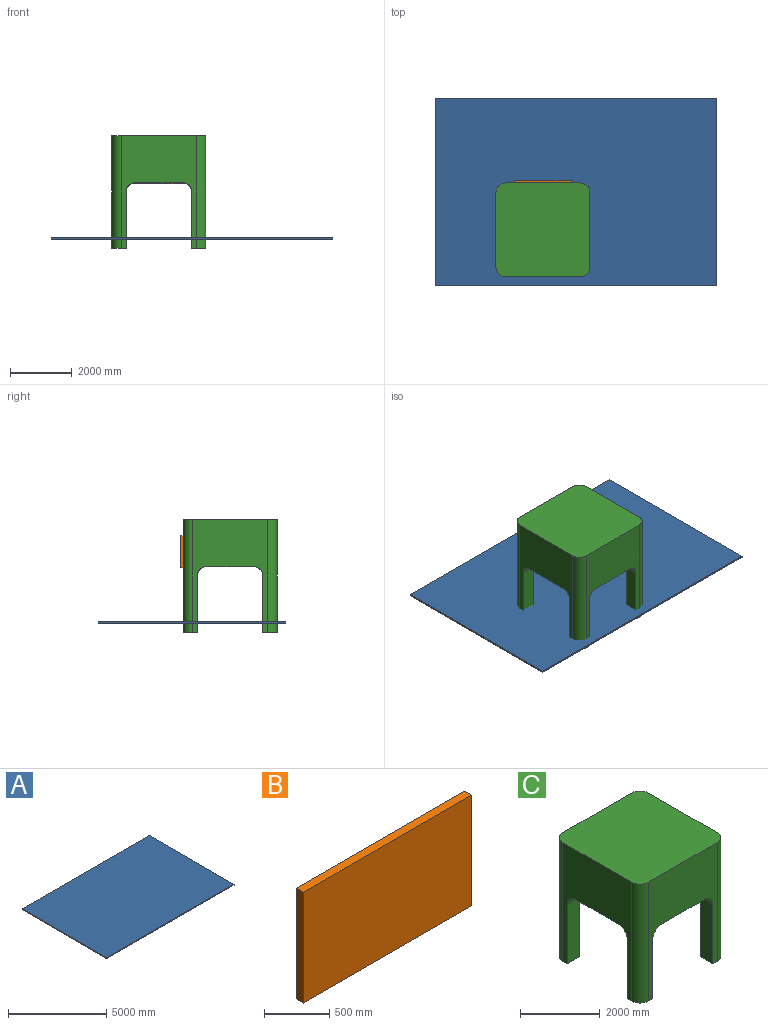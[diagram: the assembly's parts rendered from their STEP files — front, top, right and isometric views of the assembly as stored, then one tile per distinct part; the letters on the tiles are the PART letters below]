
ASSEMBLY  parts=3 mates=3
PART A: 6 faces, bbox 9144x6096x50.8 mm
  f0: plane 9144x50.8mm, normal (0,1,0), area 464515.2mm2, adj f1,f3,f4,f5
  f1: plane 6096x50.8mm, normal (-1,0,0), area 309676.8mm2, adj f0,f2,f4,f5
  f2: plane 9144x50.8mm, normal (0,-1,0), area 464515.2mm2, adj f1,f3,f4,f5
  f3: plane 6096x50.8mm, normal (1,0,0), area 309676.8mm2, adj f0,f2,f4,f5
  f4: plane 9144x6096mm, normal (0,0,1), area 55741824mm2, adj f0,f1,f2,f3
  f5: plane 9144x6096mm, normal (0,0,-1), area 55741824mm2, adj f0,f1,f2,f3
PART B: 6 faces, bbox 1828.8x76.2x1041.4 mm
  f0: plane 1041.4x76.2mm, normal (-1,0,0), area 79354.7mm2, adj f1,f3,f4,f5
  f1: plane 1828.8x76.2mm, normal (0,0,-1), area 139354.6mm2, adj f0,f2,f4,f5
  f2: plane 1041.4x76.2mm, normal (1,0,0), area 79354.7mm2, adj f1,f3,f4,f5
  f3: plane 1828.8x76.2mm, normal (0,0,1), area 139354.6mm2, adj f0,f2,f4,f5
  f4: plane 1828.8x1041.4mm, normal (0,-1,0), area 1904512.3mm2, adj f0,f1,f2,f3
  f5: plane 1828.8x1041.4mm, normal (0,1,0), area 1904512.3mm2, adj f0,f1,f2,f3
PART C: 30 faces, bbox 3048x3048x3657.6 mm
  f0: plane 457.2x457.2mm, normal (0,0,-1), area 189094.7mm2, adj f7,f8,f13,f15,f21
  f1: plane 457.2x457.2mm, normal (0,0,-1), area 189094.7mm2, adj f2,f8,f14,f16,f19
  f2: plane 3657.6x2438.4mm, normal (0,1,0), area 4406317.2mm2, adj f1,f9,f10,f11,f14,f17,f18,f19
  f3: plane 1828.8x457.2mm, normal (0,1,0), area 836127.4mm2, adj f5,f6,f20,f23
  f4: plane 1828.8x457.2mm, normal (0,-1,0), area 836127.4mm2, adj f6,f10,f18,f27
  f5: plane 457.2x457.2mm, normal (0,0,-1), area 189094.7mm2, adj f3,f6,f7,f12,f20
  f6: plane 3657.6x2438.4mm, normal (-1,0,0), area 4406317.2mm2, adj f3,f4,f5,f9,f10,f11,f12,f17
  f7: plane 3657.6x2438.4mm, normal (0,-1,0), area 4406317.2mm2, adj f0,f5,f9,f12,f13,f17,f20,f21
  f8: plane 3657.6x2438.4mm, normal (1,0,0), area 4406317.2mm2, adj f0,f1,f9,f13,f14,f15,f16,f17
  f9: plane 3048x3048mm, normal (0,0,1), area 9210555.3mm2, adj f2,f6,f7,f8,f11,f12,f13,f14
  f10: plane 457.2x457.2mm, normal (0,0,-1), area 189094.7mm2, adj f2,f4,f6,f11,f18
  f11: cylinder r=304.8mm len=3657.6mm, axis (0,0,1), area 1751181mm2, adj f2,f6,f9,f10
  f12: cylinder r=304.8mm len=3657.6mm, axis (0,0,-1), area 1751181mm2, adj f5,f6,f7,f9
  f13: cylinder r=304.8mm len=3657.6mm, axis (0,0,1), area 1751181mm2, adj f0,f7,f8,f9
  f14: cylinder r=304.8mm len=3657.6mm, axis (0,0,-1), area 1751181mm2, adj f1,f2,f8,f9
  f15: plane 1828.8x457.2mm, normal (0,1,0), area 836127.4mm2, adj f0,f8,f21,f24
  f16: plane 1828.8x457.2mm, normal (0,-1,0), area 836127.4mm2, adj f1,f8,f19,f28
  f17: plane 3048x3048mm, normal (0,0,-1), area 6967728mm2, adj f2,f6,f7,f8,f22,f23,f24,f25
  f18: plane 1828.8x457.2mm, normal (1,0,0), area 836127.4mm2, adj f2,f4,f10,f26
  f19: plane 1828.8x457.2mm, normal (-1,0,0), area 836127.4mm2, adj f1,f2,f16,f29
  f20: plane 1828.8x457.2mm, normal (1,0,0), area 836127.4mm2, adj f3,f5,f7,f22
  f21: plane 1828.8x457.2mm, normal (-1,0,0), area 836127.4mm2, adj f0,f7,f15,f25
  f22: cylinder r=304.8mm len=762mm, axis (0,1,0), area 271926.3mm2, adj f7,f17,f20,f23
  f23: cylinder r=304.8mm len=762mm, axis (-1,0,0), area 271926.3mm2, adj f3,f6,f17,f22
  f24: cylinder r=304.8mm len=762mm, axis (-1,0,0), area 271926.3mm2, adj f8,f15,f17,f25
  f25: cylinder r=304.8mm len=762mm, axis (0,-1,0), area 271926.3mm2, adj f7,f17,f21,f24
  f26: cylinder r=304.8mm len=762mm, axis (0,1,0), area 271926.3mm2, adj f2,f17,f18,f27
  f27: cylinder r=304.8mm len=762mm, axis (1,0,0), area 271926.3mm2, adj f4,f6,f17,f26
  f28: cylinder r=304.8mm len=762mm, axis (1,0,0), area 271926.3mm2, adj f8,f16,f17,f29
  f29: cylinder r=304.8mm len=762mm, axis (0,-1,0), area 271926.3mm2, adj f2,f17,f19,f28
PLACE A t=(-1501.34,688.67,-801.1)mm
PLACE B t=(-3462.67,2213.68,998.82)mm
PLACE C t=(-2548.27,613.48,-1098.66)mm
MATE parallel C.f17 <-> B.f1  axis (0,0,-1) through (-2548.27,2137.48,1034.94)mm
MATE parallel C.f1 <-> A.f4  axis (0,0,-1) through (-1269.8,1891.96,-1098.66)mm
MATE fastened C.f2 <-> B.f4  axis (0,1,0) through (-2548.27,2137.48,1519.52)mm
